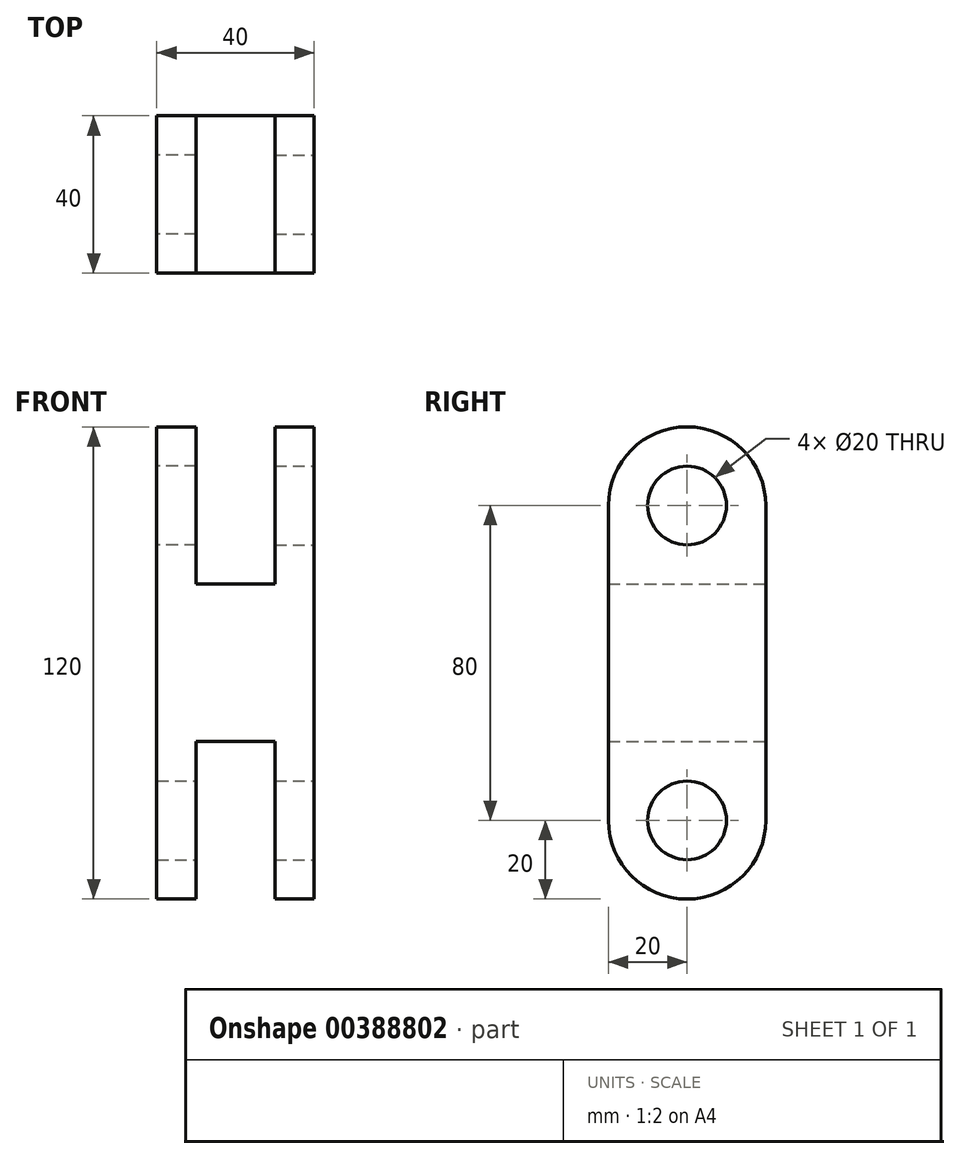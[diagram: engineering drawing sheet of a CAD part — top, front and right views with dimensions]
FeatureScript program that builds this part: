
annotation { "Feature Type Name" : "Feature", "Feature Type Description" : "" }
export const myFeature = defineFeature(function(context is Context, id is Id, definition is map)
    precondition{}
    {
        {
            var Q0;
            Q0=qCreatedBy(makeId("Right.planeOp"),FACE);
            var sketch = newSketch(context, id + "F0", { "sketchPlane" : qUnion([Q0])});
            skLineSegment(sketch, "E0.bottom", {"start": v(0, 0) * mm, "end": v(40, 0) * mm});
            skLineSegment(sketch, "E0.top", {"start": v(0, 80) * mm, "end": v(40, 80) * mm});
            skLineSegment(sketch, "E0.left", {"start": v(0, 0) * mm, "end": v(0, 80) * mm});
            skLineSegment(sketch, "E0.right", {"start": v(40, 0) * mm, "end": v(40, 80) * mm});
            skSolve(sketch);
        }
        {
            var Q0;
            Q0 = qSketchRegion(id + "F0", true);
            extrude(context, id + "F1", {"entities" : qUnion([Q0]), "depth" : 20 * mm});
        }
        {
            var Q0;
            Q0=makeQuery(id+"F1.opExtrude","CAP_FACE",FACE,{"disambiguationData":[OSD([sQuery(id+"F0.wireOp",EDGE,"E0.bottom"),sQuery(id+"F0.wireOp",EDGE,"E0.top"),sQuery(id+"F0.wireOp",EDGE,"E0.left"),sQuery(id+"F0.wireOp",EDGE,"E0.right")])],"isStart":false});
            var sketch = newSketch(context, id + "F2", { "sketchPlane" : qUnion([Q0])});
            skLineSegment(sketch, "E1.bottom", {"start": v(0, 80) * mm, "end": v(40, 80) * mm});
            skLineSegment(sketch, "E1.left", {"start": v(0, 80) * mm, "end": v(0, 100) * mm});
            skLineSegment(sketch, "E1.right", {"start": v(40, 80) * mm, "end": v(40, 100) * mm});
            skArc(sketch, "E2", {"start": v(40, 100) * mm, "mid": v(20, 120) * mm, "end": v(0, 100) * mm});
            skCircle(sketch, "E3", {"center": v(20, 100) * mm, "radius": 10 * mm});
            skSolve(sketch);
        }
        {
            var Q0;
            Q0 = qSketchRegion(id + "F2", true);
            extrude(context, id + "F3", {"entities" : qUnion([Q0]), "operationType" : NewBodyOperationType.ADD, "oppositeDirection" : true, "depth" : 10 * mm});
        }
        {
            var Q0;
            Q0=makeQuery(id+"F1.opExtrude","SWEPT_BODY",BODY,{"disambiguationData":[OSD([sQuery(id+"F0.wireOp",EDGE,"E0.bottom"),sQuery(id+"F0.wireOp",EDGE,"E0.top"),sQuery(id+"F0.wireOp",EDGE,"E0.left"),sQuery(id+"F0.wireOp",EDGE,"E0.right")])]});
            var Q1;
            Q1=makeQuery(id+"F1.opExtrude","CAP_FACE",FACE,{"disambiguationData":[OSD([sQuery(id+"F0.wireOp",EDGE,"E0.bottom"),sQuery(id+"F0.wireOp",EDGE,"E0.top"),sQuery(id+"F0.wireOp",EDGE,"E0.left"),sQuery(id+"F0.wireOp",EDGE,"E0.right")])],"isStart":true});
            mirror(context, id + "F4", {"operationType" : NewBodyOperationType.ADD, "entities" : qUnion([Q0]), "mirrorPlane" : qUnion([Q1])});
        }
        {
            var Q0;
            {var subQ0=makeQuery(id+"F3.boolean.opBoolean","MERGE",FACE,{"derivedFrom":[makeQuery(id+"F1.opExtrude","SWEPT_FACE",FACE,{"disambiguationData":[OSD([sQuery(id+"F0.wireOp",EDGE,"E0.right")])]}),makeQuery(id+"F3.opExtrude","SWEPT_FACE",FACE,{"disambiguationData":[OSD([sQuery(id+"F2.wireOp",EDGE,"E1.right")])]})]});Q0=makeQuery(id+"F4.boolean.opBoolean","MERGE",FACE,{"derivedFrom":[subQ0,makeQuery(id+"F4.opPattern","COPY",FACE,{"derivedFrom":subQ0,"instanceName":"1"})]});}
            var sketch = newSketch(context, id + "F5", { "sketchPlane" : qUnion([Q0])});
            skLineSegment(sketch, "E4.bottom", {"start": v(-10, 0) * mm, "end": v(10, 0) * mm});
            skLineSegment(sketch, "E4.top", {"start": v(-10, 40) * mm, "end": v(10, 40) * mm});
            skLineSegment(sketch, "E4.left", {"start": v(-10, 0) * mm, "end": v(-10, 40) * mm});
            skLineSegment(sketch, "E4.right", {"start": v(10, 0) * mm, "end": v(10, 40) * mm});
            skSolve(sketch);
        }
        {
            var Q0;
            Q0 = qSketchRegion(id + "F5", true);
            var Q1;
            {var subQ0=makeQuery(id+"F3.boolean.opBoolean","MERGE",FACE,{"derivedFrom":[makeQuery(id+"F1.opExtrude","SWEPT_FACE",FACE,{"disambiguationData":[OSD([sQuery(id+"F0.wireOp",EDGE,"E0.left")])]}),makeQuery(id+"F3.opExtrude","SWEPT_FACE",FACE,{"disambiguationData":[OSD([sQuery(id+"F2.wireOp",EDGE,"E1.left")])]})]});Q1=makeQuery(id+"F4.boolean.opBoolean","MERGE",FACE,{"derivedFrom":[subQ0,makeQuery(id+"F4.opPattern","COPY",FACE,{"derivedFrom":subQ0,"instanceName":"1"})]});}
            extrude(context, id + "F6", {"entities" : qUnion([Q0]), "operationType" : NewBodyOperationType.REMOVE, "endBound" : BoundingType.UP_TO_SURFACE, "oppositeDirection" : true, "endBoundEntityFace" : qUnion([Q1]), "depth" : 25 * mm});
        }
        {
            var Q0;
            Q0=makeQuery(id+"F3.boolean.opBoolean","MERGE",FACE,{"derivedFrom":[makeQuery(id+"F1.opExtrude","CAP_FACE",FACE,{"disambiguationData":[OSD([sQuery(id+"F0.wireOp",EDGE,"E0.bottom"),sQuery(id+"F0.wireOp",EDGE,"E0.top"),sQuery(id+"F0.wireOp",EDGE,"E0.left"),sQuery(id+"F0.wireOp",EDGE,"E0.right")])],"isStart":false}),makeQuery(id+"F3.opExtrude","CAP_FACE",FACE,{"disambiguationData":[OSD([sQuery(id+"F2.wireOp",EDGE,"E1.bottom"),sQuery(id+"F2.wireOp",EDGE,"E1.left"),sQuery(id+"F2.wireOp",EDGE,"E1.right"),sQuery(id+"F2.wireOp",EDGE,"E2"),sQuery(id+"F2.wireOp",EDGE,"E3")])],"isStart":true})]});
            var sketch = newSketch(context, id + "F7", { "sketchPlane" : qUnion([Q0])});
            skLineSegment(sketch, "E5", {"start": v(20, 0) * mm, "end": v(20, 20) * mm, "construction": true});
            skCircle(sketch, "E6", {"center": v(20, 20) * mm, "radius": 10 * mm});
            skSolve(sketch);
        }
        {
            var Q0;
            Q0 = qSketchRegion(id + "F7", true);
            var Q1;
            Q1=makeQuery(id+"F4.opPattern","COPY",FACE,{"derivedFrom":makeQuery(id+"F3.boolean.opBoolean","MERGE",FACE,{"derivedFrom":[makeQuery(id+"F1.opExtrude","CAP_FACE",FACE,{"disambiguationData":[OSD([sQuery(id+"F0.wireOp",EDGE,"E0.bottom"),sQuery(id+"F0.wireOp",EDGE,"E0.top"),sQuery(id+"F0.wireOp",EDGE,"E0.left"),sQuery(id+"F0.wireOp",EDGE,"E0.right")])],"isStart":false}),makeQuery(id+"F3.opExtrude","CAP_FACE",FACE,{"disambiguationData":[OSD([sQuery(id+"F2.wireOp",EDGE,"E1.bottom"),sQuery(id+"F2.wireOp",EDGE,"E1.left"),sQuery(id+"F2.wireOp",EDGE,"E1.right"),sQuery(id+"F2.wireOp",EDGE,"E2"),sQuery(id+"F2.wireOp",EDGE,"E3")])],"isStart":true})]}),"instanceName":"1"});
            extrude(context, id + "F8", {"entities" : qUnion([Q0]), "operationType" : NewBodyOperationType.REMOVE, "endBound" : BoundingType.UP_TO_SURFACE, "oppositeDirection" : true, "endBoundEntityFace" : qUnion([Q1]), "depth" : 25 * mm});
        }
        {
            var Q0;
            {var subQ2=sQuery(id+"F0.wireOp",EDGE,"E0.left");var subQ4=sQuery(id+"F0.wireOp",EDGE,"E0.bottom");var subQ6=makeQuery(id+"F1.opExtrude","SWEPT_EDGE",EDGE,{"disambiguationData":[OSD([subQ4,subQ2])]});Q0=makeQuery(id+"F6.boolean.opBoolean","SPLIT",EDGE,{"disambiguationData":[TD([makeQuery(id+"F6.opExtrude","SWEPT_FACE",FACE,{"disambiguationData":[OSD([sQuery(id+"F5.wireOp",EDGE,"E4.right")])]})])],"derivedFrom":makeQuery(id+"F4.boolean.opBoolean","MERGE",EDGE,{"derivedFrom":[subQ6,makeQuery(id+"F4.opPattern","COPY",EDGE,{"derivedFrom":subQ6,"instanceName":"1"})]})});}
            fillet(context, id + "F9", {"entities" : qUnion([Q0]), "radius" : 20 * mm, "tangentPropagation" : true, "allowEdgeOverflow" : false});
        }
        {
            var Q0;
            {var subQ2=sQuery(id+"F0.wireOp",EDGE,"E0.right");var subQ4=sQuery(id+"F0.wireOp",EDGE,"E0.bottom");var subQ6=makeQuery(id+"F1.opExtrude","SWEPT_EDGE",EDGE,{"disambiguationData":[OSD([subQ4,subQ2])]});Q0=makeQuery(id+"F6.boolean.opBoolean","SPLIT",EDGE,{"disambiguationData":[TD([makeQuery(id+"F6.opExtrude","SWEPT_FACE",FACE,{"disambiguationData":[OSD([sQuery(id+"F5.wireOp",EDGE,"E4.right")])]})])],"derivedFrom":makeQuery(id+"F4.boolean.opBoolean","MERGE",EDGE,{"derivedFrom":[subQ6,makeQuery(id+"F4.opPattern","COPY",EDGE,{"derivedFrom":subQ6,"instanceName":"1"})]})});}
            var Q1;
            {var subQ1=sQuery(id+"F0.wireOp",EDGE,"E0.right");var subQ2=sQuery(id+"F0.wireOp",EDGE,"E0.bottom");var subQ6=makeQuery(id+"F1.opExtrude","SWEPT_EDGE",EDGE,{"disambiguationData":[OSD([subQ2,subQ1])]});Q1=makeQuery(id+"F6.boolean.opBoolean","SPLIT",EDGE,{"disambiguationData":[TD([makeQuery(id+"F6.opExtrude","SWEPT_FACE",FACE,{"disambiguationData":[OSD([sQuery(id+"F5.wireOp",EDGE,"E4.left")])]})])],"derivedFrom":makeQuery(id+"F4.boolean.opBoolean","MERGE",EDGE,{"derivedFrom":[subQ6,makeQuery(id+"F4.opPattern","COPY",EDGE,{"derivedFrom":subQ6,"instanceName":"1"})]})});}
            var Q2;
            {var subQ1=sQuery(id+"F0.wireOp",EDGE,"E0.left");var subQ2=sQuery(id+"F0.wireOp",EDGE,"E0.bottom");var subQ6=makeQuery(id+"F1.opExtrude","SWEPT_EDGE",EDGE,{"disambiguationData":[OSD([subQ2,subQ1])]});Q2=makeQuery(id+"F6.boolean.opBoolean","SPLIT",EDGE,{"disambiguationData":[TD([makeQuery(id+"F6.opExtrude","SWEPT_FACE",FACE,{"disambiguationData":[OSD([sQuery(id+"F5.wireOp",EDGE,"E4.left")])]})])],"derivedFrom":makeQuery(id+"F4.boolean.opBoolean","MERGE",EDGE,{"derivedFrom":[subQ6,makeQuery(id+"F4.opPattern","COPY",EDGE,{"derivedFrom":subQ6,"instanceName":"1"})]})});}
            fillet(context, id + "F10", {"entities" : qUnion([Q0, Q1, Q2]), "radius" : 20 * mm, "tangentPropagation" : true, "allowEdgeOverflow" : false});
        }
    });
